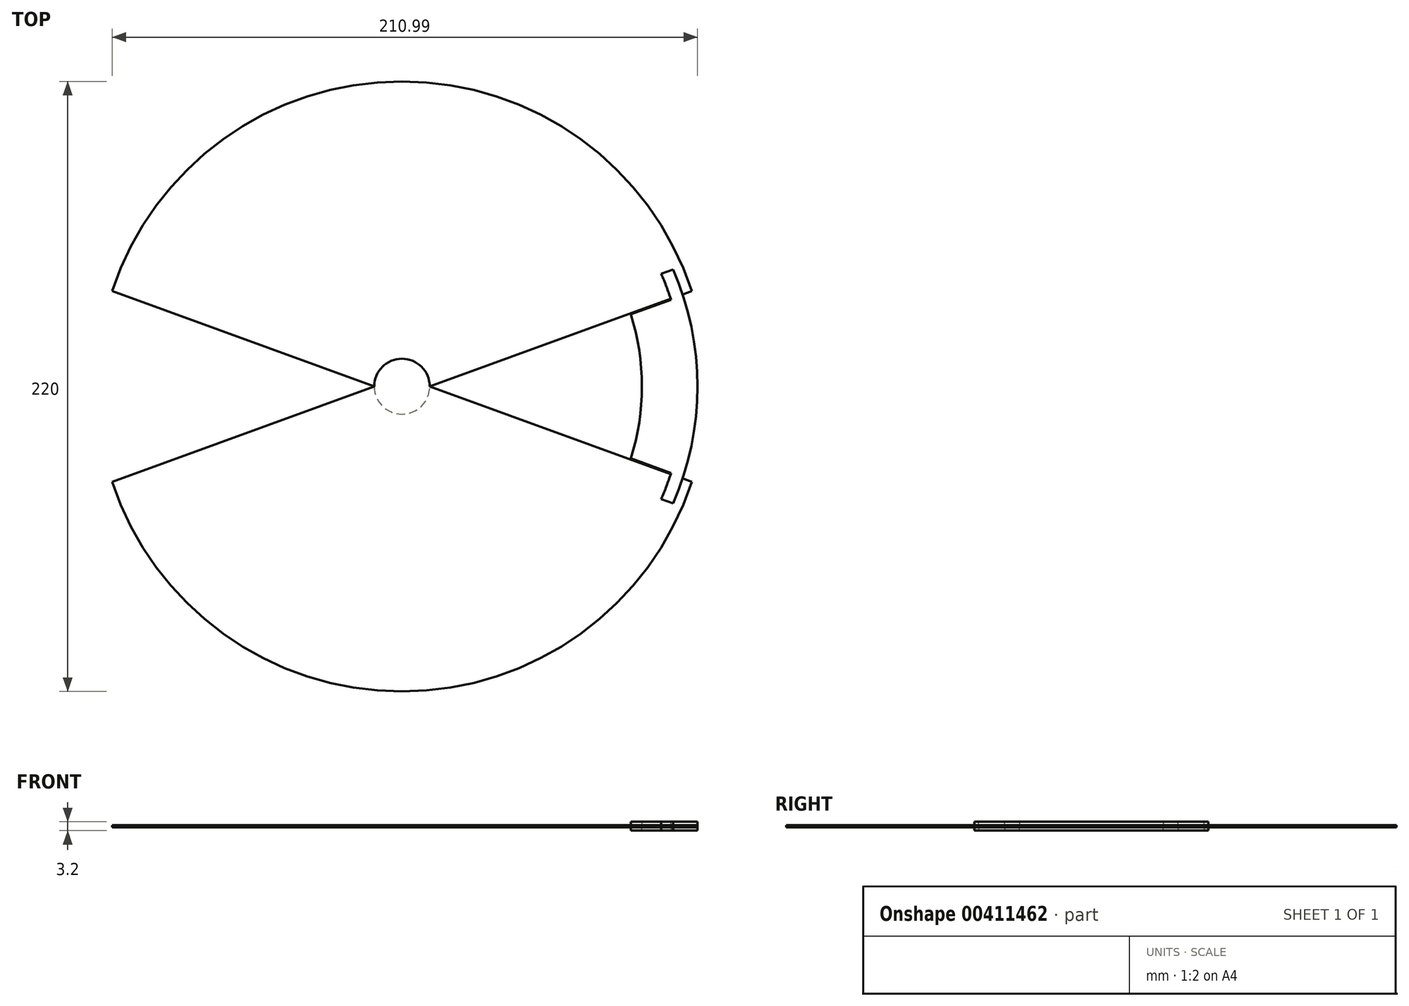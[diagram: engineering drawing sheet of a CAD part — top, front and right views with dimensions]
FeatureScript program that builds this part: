
annotation { "Feature Type Name" : "Feature", "Feature Type Description" : "" }
export const myFeature = defineFeature(function(context is Context, id is Id, definition is map)
    precondition{}
    {
        {
            var Q0;
            Q0=qCreatedBy(makeId("Top.planeOp"),FACE);
            var sketch = newSketch(context, id + "F0", { "sketchPlane" : qUnion([Q0])});
            skArc(sketch, "E0", {"start": v(104.49, 34.4) * mm, "mid": v(0, 110) * mm, "end": v(-104.49, 34.4) * mm});
            skArc(sketch, "E1", {"start": v(10, 0) * mm, "mid": v(0, 10) * mm, "end": v(-10, 0) * mm});
            skLineSegment(sketch, "E2", {"start": v(10, 0) * mm, "end": v(104.49, 34.4) * mm});
            skLineSegment(sketch, "E3.MirrorCS", {"start": v(-10, 0) * mm, "end": v(-104.49, 34.4) * mm});
            skSolve(sketch);
        }
        {
            var Q0;
            Q0 = qSketchRegion(id + "F0", true);
            extrude(context, id + "F1", {"entities" : qUnion([Q0]), "depth" : .8 * mm, "offsetDistance" : 25 * mm});
        }
        {
            var Q0;
            Q0=qCreatedBy(makeId("Top.planeOp"),FACE);
            var sketch = newSketch(context, id + "F2", { "sketchPlane" : qUnion([Q0])});
            skCircle(sketch, "E4", {"center": v(0, 0) * mm, "radius": 10 * mm});
            skSolve(sketch);
        }
        {
            var Q0;
            Q0 = qSketchRegion(id + "F2", true);
            extrude(context, id + "F3", {"entities" : qUnion([Q0]), "operationType" : NewBodyOperationType.ADD, "depth" : .4 * mm, "offsetDistance" : 25 * mm});
        }
        {
            var Q0;
            Q0=qCreatedBy(makeId("Top.planeOp"),FACE);
            var sketch = newSketch(context, id + "F4", { "sketchPlane" : qUnion([Q0])});
            skArc(sketch, "E5", {"start": v(101.32, -32.81) * mm, "mid": v(106.5, 0) * mm, "end": v(101.32, 32.81) * mm});
            skArc(sketch, "E6", {"start": v(80.95, -30.47) * mm, "mid": v(86.47, -2.39) * mm, "end": v(82.51, 25.97) * mm});
            skPoint(sketch, "E7.orphan", {"position": v(15, 0) * mm});
            skLineSegment(sketch, "E8", {"start": v(82.51, 25.97) * mm, "end": v(101.32, 32.81) * mm});
            skLineSegment(sketch, "E9.MirrorCS", {"start": v(82.51, -25.97) * mm, "end": v(101.32, -32.81) * mm});
            skSolve(sketch);
        }
        {
            var Q0;
            Q0 = qSketchRegion(id + "F4", true);
            extrude(context, id + "F5", {"entities" : qUnion([Q0]), "depth" : 2 * mm, "offsetDistance" : 25 * mm});
        }
        {
            var Q0;
            Q0=makeQuery(id+"F5.opExtrude","CAP_FACE",FACE,{"disambiguationData":[OSD([sQuery(id+"F4.wireOp",EDGE,"E5"),sQuery(id+"F4.wireOp",EDGE,"E6"),sQuery(id+"F4.wireOp",EDGE,"80C2W4JD-9Spr-5qMN-Q4De-XfFfzPM6A9mv"),sQuery(id+"F4.wireOp",EDGE,"6bd955d4-5a4a-4057-a4fd-fc1f6c9fed490.MirrorCS")])],"isStart":false});
            var sketch = newSketch(context, id + "F6", { "sketchPlane" : qUnion([Q0])});
            skArc(sketch, "E10", {"start": v(97.8, -42.17) * mm, "mid": v(106.5, 0) * mm, "end": v(97.8, 42.17) * mm});
            skArc(sketch, "E11", {"start": v(93.46, -40.6) * mm, "mid": v(101.9, 0) * mm, "end": v(93.46, 40.6) * mm});
            skLineSegment(sketch, "E12", {"start": v(93.46, 40.6) * mm, "end": v(97.8, 42.17) * mm});
            skLineSegment(sketch, "E13.MirrorCS", {"start": v(93.46, -40.6) * mm, "end": v(97.8, -42.17) * mm});
            skSolve(sketch);
        }
        {
            var Q0;
            Q0 = qSketchRegion(id + "F6", true);
            var Q1;
            Q1=makeQuery(id+"F5.opExtrude","CAP_FACE",FACE,{"disambiguationData":[OSD([sQuery(id+"F4.wireOp",EDGE,"E5"),sQuery(id+"F4.wireOp",EDGE,"E6"),sQuery(id+"F4.wireOp",EDGE,"80C2W4JD-9Spr-5qMN-Q4De-XfFfzPM6A9mv"),sQuery(id+"F4.wireOp",EDGE,"6bd955d4-5a4a-4057-a4fd-fc1f6c9fed490.MirrorCS")])],"isStart":true});
            extrude(context, id + "F7", {"entities" : qUnion([Q0]), "operationType" : NewBodyOperationType.ADD, "endBound" : BoundingType.UP_TO_SURFACE, "oppositeDirection" : true, "depth" : 2 * mm, "endBoundEntityFace" : qUnion([Q1]), "offsetDistance" : 25 * mm});
        }
        {
            var Q0;
            Q0=makeQuery(id+"F3.opExtrude","CAP_FACE",FACE,{"disambiguationData":[OSD([sQuery(id+"F2.wireOp",EDGE,"E4")])],"isStart":false});
            cPlane(context, id + "F8", {"entities" : qUnion([Q0]), "cplaneType" : CPlaneType.OFFSET, "offset" : 0 * mm, "width" : 150 * mm, "height" : 150 * mm});
        }
        {
            var Q0;
            Q0=qCreatedBy(id+"F8.planeOp",FACE);
            var sketch = newSketch(context, id + "F9", { "sketchPlane" : qUnion([Q0])});
            skLineSegment(sketch, "E14", {"start": v(-70.66, 0) * mm, "end": v(70.26, 0) * mm});
            skLineSegment(sketch, "E15", {"start": v(0, -26.1) * mm, "end": v(0, 31.72) * mm});
            skSolve(sketch);
        }
        {
            var Q0;
            Q0=makeQuery(id+"F1.opExtrude","SWEPT_BODY",BODY,{"disambiguationData":[OSD([sQuery(id+"F0.wireOp",EDGE,"E0"),sQuery(id+"F0.wireOp",EDGE,"E1"),sQuery(id+"F0.wireOp",EDGE,"E2"),sQuery(id+"F0.wireOp",EDGE,"E3.MirrorCS")])]});
            var Q1;
            Q1=sQuery(id+"F9.wireOp",EDGE,"E14");
            transform(context, id + "F10", {"entities" : qUnion([Q0]), "transformType" : TransformType.ROTATION, "transformAxis" : qUnion([Q1]), "angle" : 180 * degree, "makeCopy" : true});
        }
    });
